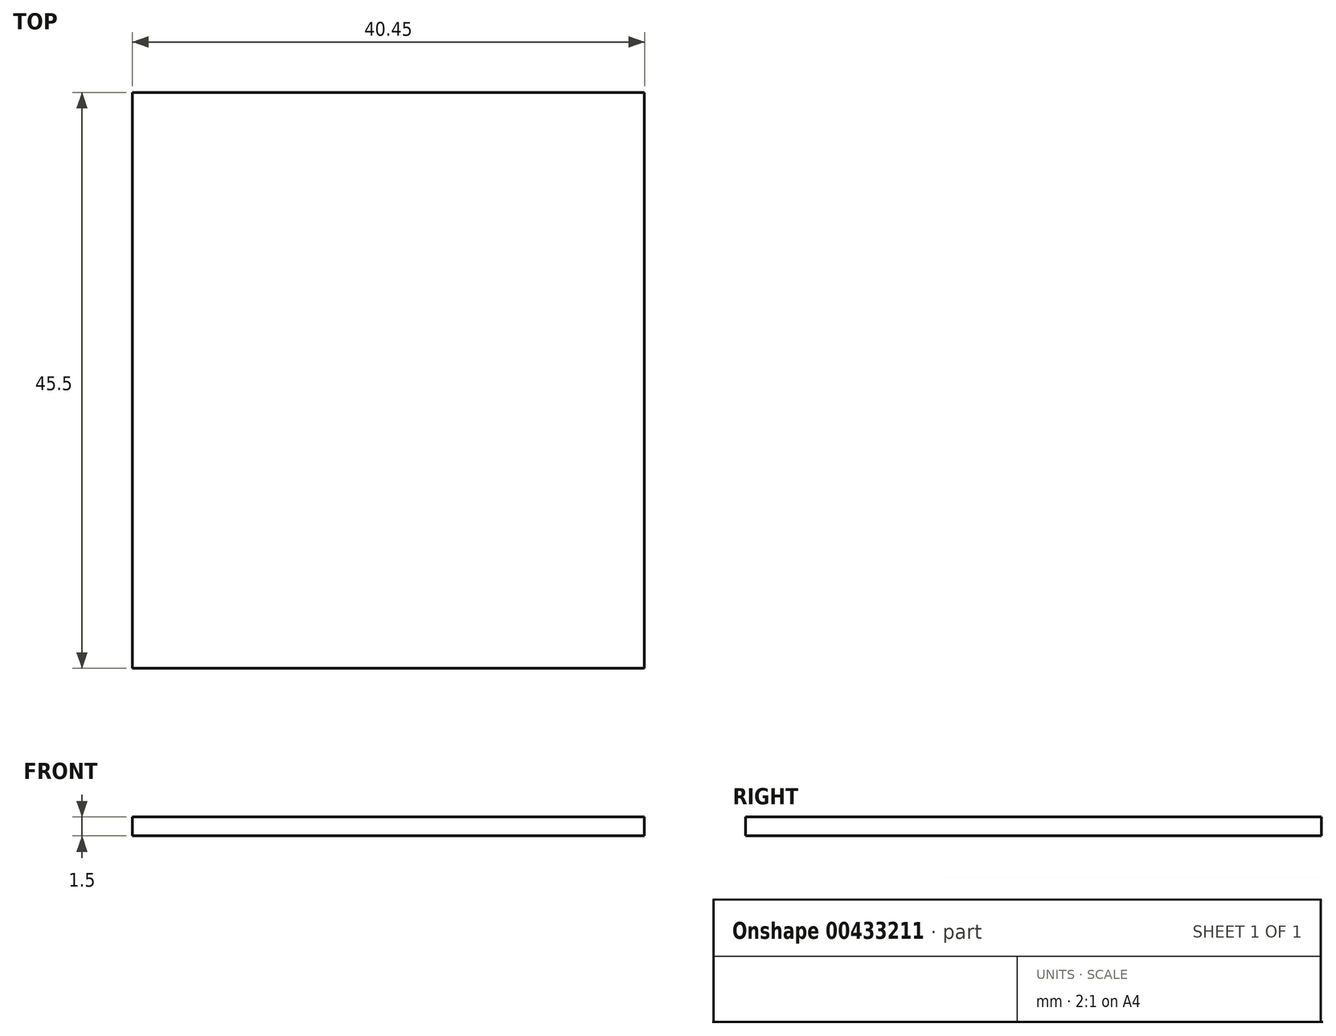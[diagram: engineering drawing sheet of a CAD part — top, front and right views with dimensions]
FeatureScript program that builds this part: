
annotation { "Feature Type Name" : "Feature", "Feature Type Description" : "" }
export const myFeature = defineFeature(function(context is Context, id is Id, definition is map)
    precondition{}
    {
        {
            var Q0;
            Q0=qCreatedBy(makeId("Top.planeOp"),FACE);
            var sketch = newSketch(context, id + "F0", { "sketchPlane" : qUnion([Q0])});
            skLineSegment(sketch, "E0.bottom", {"start": v(40.45, 45.5) * mm, "end": v(0, 45.5) * mm});
            skLineSegment(sketch, "E0.top", {"start": v(40.45, 0) * mm, "end": v(0, 0) * mm});
            skLineSegment(sketch, "E0.left", {"start": v(40.45, 45.5) * mm, "end": v(40.45, 0) * mm});
            skLineSegment(sketch, "E0.right", {"start": v(0, 45.5) * mm, "end": v(0, 0) * mm});
            skLineSegment(sketch, "E1.bottom", {"start": v(40.45, 45.5) * mm, "end": v(0, 45.5) * mm, "construction": true});
            skLineSegment(sketch, "E1.top", {"start": v(40.45, 0) * mm, "end": v(0, 0) * mm, "construction": true});
            skLineSegment(sketch, "E1.left", {"start": v(40.45, 45.5) * mm, "end": v(40.45, 0) * mm, "construction": true});
            skLineSegment(sketch, "E1.right", {"start": v(0, 45.5) * mm, "end": v(0, 0) * mm, "construction": true});
            skLineSegment(sketch, "E2.bottom", {"start": v(40.45, 45.5) * mm, "end": v(40.45, 45.5) * mm});
            skLineSegment(sketch, "E2.top", {"start": v(40.45, 45.5) * mm, "end": v(40.45, 45.5) * mm});
            skLineSegment(sketch, "E2.left", {"start": v(40.45, 45.5) * mm, "end": v(40.45, 45.5) * mm});
            skLineSegment(sketch, "E2.right", {"start": v(40.45, 45.5) * mm, "end": v(40.45, 45.5) * mm});
            skSolve(sketch);
        }
        {
            var Q0;
            Q0=makeQuery(id+"F0.imprint","IMPRINT",FACE,{"disambiguationData":[TD([[makeQuery(id+"F0.imprint","IMPRINT",EDGE,{"derivedFrom":sQuery(id+"F0.wireOp",EDGE,"E0.bottom")}),1.0]])]});
            var sketch = newSketch(context, id + "F1", { "sketchPlane" : qUnion([Q0])});
            skSolve(sketch);
        }
        {
            var Q0;
            Q0 = qSketchRegion(id + "F1", true);
            var Q1;
            Q1=makeQuery(id+"F0.imprint","IMPRINT",FACE,{"disambiguationData":[TD([[makeQuery(id+"F0.imprint","IMPRINT",EDGE,{"derivedFrom":sQuery(id+"F0.wireOp",EDGE,"E0.bottom")}),1.0]])]});
            extrude(context, id + "F2", {"entities" : qUnion([Q0, Q1]), "depth" : 1.5 * mm});
        }
    });
